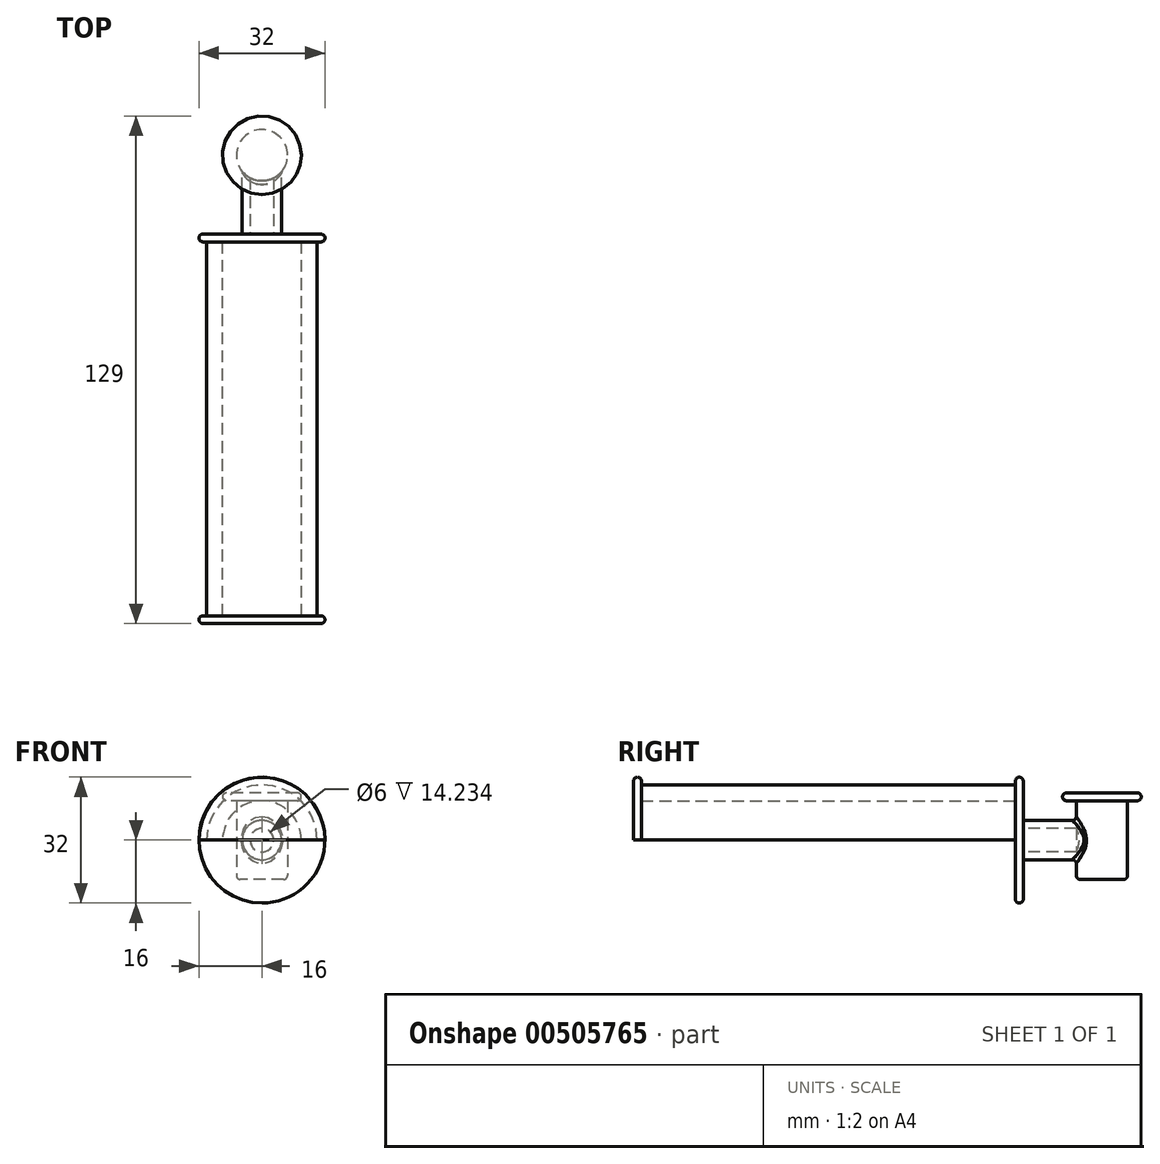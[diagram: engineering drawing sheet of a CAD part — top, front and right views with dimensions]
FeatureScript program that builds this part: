
annotation { "Feature Type Name" : "Feature", "Feature Type Description" : "" }
export const myFeature = defineFeature(function(context is Context, id is Id, definition is map)
    precondition{}
    {
        {
            var Q0;
            Q0=qCreatedBy(makeId("Top.planeOp"),FACE);
            var sketch = newSketch(context, id + "F0", { "sketchPlane" : qUnion([Q0])});
            skCircle(sketch, "E0", {"center": v(0, 0) * mm, "radius": 6.5 * mm});
            skSolve(sketch);
        }
        {
            var Q0;
            Q0 = qSketchRegion(id + "F0", true);
            extrude(context, id + "F1", {"entities" : qUnion([Q0]), "endBound" : BoundingType.SYMMETRIC, "depth" : 20 * mm});
        }
        {
            var Q0;
            Q0=makeQuery(id+"F1.opExtrude","CAP_FACE",FACE,{"disambiguationData":[OSD([sQuery(id+"F0.wireOp",EDGE,"E0")])],"isStart":false});
            var sketch = newSketch(context, id + "F2", { "sketchPlane" : qUnion([Q0])});
            skCircle(sketch, "E1", {"center": v(0, 0) * mm, "radius": 10 * mm});
            skSolve(sketch);
        }
        {
            var Q0;
            Q0 = qSketchRegion(id + "F2", true);
            extrude(context, id + "F3", {"entities" : qUnion([Q0]), "operationType" : NewBodyOperationType.ADD, "depth" : 2 * mm});
        }
        {
            var Q0;
            Q0=makeQuery(id+"F1.opExtrude","CAP_FACE",FACE,{"disambiguationData":[OSD([sQuery(id+"F0.wireOp",EDGE,"E0")])],"isStart":true});
            var sketch = newSketch(context, id + "F4", { "sketchPlane" : qUnion([Q0])});
            skCircle(sketch, "E2", {"center": v(0, 0) * mm, "radius": 10 * mm});
            skSolve(sketch);
        }
        {
            var Q0;
            Q0=qCreatedBy(makeId("Front.planeOp"),FACE);
            var sketch = newSketch(context, id + "F5", { "sketchPlane" : qUnion([Q0])});
            skCircle(sketch, "E3", {"center": v(0, 0) * mm, "radius": 5 * mm});
            skSolve(sketch);
        }
        {
            var Q0;
            Q0 = qSketchRegion(id + "F5", true);
            extrude(context, id + "F6", {"entities" : qUnion([Q0]), "operationType" : NewBodyOperationType.ADD, "depth" : 20 * mm});
        }
        {
            var Q0;
            Q0=makeQuery(id+"F6.opExtrude","CAP_FACE",FACE,{"disambiguationData":[OSD([sQuery(id+"F5.wireOp",EDGE,"E3")])],"isStart":false});
            var sketch = newSketch(context, id + "F7", { "sketchPlane" : qUnion([Q0])});
            skCircle(sketch, "E4", {"center": v(0, 0) * mm, "radius": 3 * mm});
            skSolve(sketch);
        }
        {
            var Q0;
            Q0 = qSketchRegion(id + "F7", true);
            var Q1;
            Q1=makeQuery(id+"F1.opExtrude","SWEPT_FACE",FACE,{"disambiguationData":[OSD([sQuery(id+"F0.wireOp",EDGE,"E0")])]});
            extrude(context, id + "F8", {"entities" : qUnion([Q0]), "operationType" : NewBodyOperationType.REMOVE, "endBound" : BoundingType.UP_TO_SURFACE, "oppositeDirection" : true, "endBoundEntityFace" : qUnion([Q1]), "depth" : 25 * mm});
        }
        {
            var Q0;
            Q0=makeQuery(id+"F6.opExtrude","CAP_FACE",FACE,{"disambiguationData":[OSD([sQuery(id+"F5.wireOp",EDGE,"E3")])],"isStart":false});
            var sketch = newSketch(context, id + "F9", { "sketchPlane" : qUnion([Q0])});
            skCircle(sketch, "E5", {"center": v(0, 0) * mm, "radius": 16 * mm});
            skSolve(sketch);
        }
        {
            var Q0;
            Q0 = qSketchRegion(id + "F9", true);
            extrude(context, id + "F10", {"entities" : qUnion([Q0]), "operationType" : NewBodyOperationType.ADD, "depth" : 2 * mm});
        }
        {
            var Q0;
            Q0=makeQuery(id+"F10.opExtrude","CAP_FACE",FACE,{"disambiguationData":[OSD([sQuery(id+"F9.wireOp",EDGE,"E5")])],"isStart":false});
            var sketch = newSketch(context, id + "F11", { "sketchPlane" : qUnion([Q0])});
            skArc(sketch, "E6", {"start": v(14, 0) * mm, "mid": v(0, 14) * mm, "end": v(-14, 0) * mm});
            skLineSegment(sketch, "E7", {"start": v(-10, 0) * mm, "end": v(-14, 0) * mm});
            skLineSegment(sketch, "E8", {"start": v(10, 0) * mm, "end": v(14, 0) * mm});
            skArc(sketch, "E9.0", {"start": v(10, 0) * mm, "mid": v(0, 10) * mm, "end": v(-10, 0) * mm});
            skSolve(sketch);
        }
        {
            var Q0;
            Q0 = qSketchRegion(id + "F11", true);
            extrude(context, id + "F12", {"entities" : qUnion([Q0]), "operationType" : NewBodyOperationType.ADD, "depth" : 95 * mm});
        }
        {
            var Q0;
            Q0=makeQuery(id+"F12.opExtrude","CAP_FACE",FACE,{"disambiguationData":[OSD([sQuery(id+"F11.wireOp",EDGE,"E6"),sQuery(id+"F11.wireOp",EDGE,"E7"),sQuery(id+"F11.wireOp",EDGE,"E8"),sQuery(id+"F11.wireOp",EDGE,"E9.0")])],"isStart":false});
            var sketch = newSketch(context, id + "F13", { "sketchPlane" : qUnion([Q0])});
            skArc(sketch, "E10", {"start": v(16, 0) * mm, "mid": v(0, 16) * mm, "end": v(-16, 0) * mm});
            skLineSegment(sketch, "E11", {"start": v(0, 0) * mm, "end": v(16, 0) * mm});
            skLineSegment(sketch, "E12", {"start": v(0, 0) * mm, "end": v(-16, 0) * mm});
            skSolve(sketch);
        }
        {
            var Q0;
            Q0 = qSketchRegion(id + "F13", true);
            extrude(context, id + "F14", {"entities" : qUnion([Q0]), "operationType" : NewBodyOperationType.ADD, "depth" : 2 * mm});
        }
        {
            var Q0;
            Q0=makeQuery(id+"F1.opExtrude","CAP_EDGE",EDGE,{"disambiguationData":[OSD([sQuery(id+"F0.wireOp",EDGE,"E0")])],"isStart":false});
            var Q1;
            Q1=makeQuery(id+"F1.opExtrude","CAP_EDGE",EDGE,{"disambiguationData":[OSD([sQuery(id+"F0.wireOp",EDGE,"E0")])],"isStart":true});
            var Q2;
            Q2=makeQuery(id+"F3.opExtrude","CAP_EDGE",EDGE,{"disambiguationData":[OSD([sQuery(id+"F2.wireOp",EDGE,"E1")])],"isStart":false});
            var Q3;
            Q3=makeQuery(id+"F3.opExtrude","CAP_EDGE",EDGE,{"disambiguationData":[OSD([sQuery(id+"F2.wireOp",EDGE,"E1")])],"isStart":true});
            var Q4;
            Q4=makeQuery(id+"F7Hb1qnxx9VSfp0_1.opExtrude","CAP_EDGE",EDGE,{"disambiguationData":[OSD([sQuery(id+"F4.wireOp",EDGE,"E2")])],"isStart":true});
            var Q5;
            Q5=makeQuery(id+"F7Hb1qnxx9VSfp0_1.opExtrude","CAP_EDGE",EDGE,{"disambiguationData":[OSD([sQuery(id+"F4.wireOp",EDGE,"E2")])],"isStart":false});
            var Q6;
            Q6=makeQuery(id+"F10.opExtrude","CAP_EDGE",EDGE,{"disambiguationData":[OSD([sQuery(id+"F9.wireOp",EDGE,"E5")])],"isStart":true});
            var Q7;
            Q7=makeQuery(id+"F10.opExtrude","CAP_EDGE",EDGE,{"disambiguationData":[OSD([sQuery(id+"F9.wireOp",EDGE,"E5")])],"isStart":false});
            var Q8;
            Q8=makeQuery(id+"F6.opExtrude","CAP_EDGE",EDGE,{"disambiguationData":[OSD([sQuery(id+"F5.wireOp",EDGE,"E3")])],"isStart":false});
            var Q9;
            Q9=makeQuery(id+"F6.boolean.opBoolean","INTERSECT",EDGE,{"disambiguationData":[OD(1.0)],"derivedFrom":[makeQuery(id+"F1.opExtrude","SWEPT_FACE",FACE,{"disambiguationData":[OSD([sQuery(id+"F0.wireOp",EDGE,"E0")])]}),makeQuery(id+"F6.opExtrude","SWEPT_FACE",FACE,{"disambiguationData":[OSD([sQuery(id+"F5.wireOp",EDGE,"E3")])]})]});
            var Q10;
            Q10=makeQuery(id+"F6.boolean.opBoolean","INTERSECT",EDGE,{"disambiguationData":[OD(0.0)],"derivedFrom":[makeQuery(id+"F1.opExtrude","SWEPT_FACE",FACE,{"disambiguationData":[OSD([sQuery(id+"F0.wireOp",EDGE,"E0")])]}),makeQuery(id+"F6.opExtrude","SWEPT_FACE",FACE,{"disambiguationData":[OSD([sQuery(id+"F5.wireOp",EDGE,"E3")])]})]});
            var Q11;
            Q11=makeQuery(id+"F14.opExtrude","CAP_EDGE",EDGE,{"disambiguationData":[OSD([sQuery(id+"F13.wireOp",EDGE,"E10")])],"isStart":false});
            var Q12;
            Q12=makeQuery(id+"F14.opExtrude","CAP_EDGE",EDGE,{"disambiguationData":[OSD([sQuery(id+"F13.wireOp",EDGE,"E10")])],"isStart":true});
            var Q13;
            Q13=makeQuery(id+"F12.opExtrude","CAP_EDGE",EDGE,{"disambiguationData":[OSD([sQuery(id+"F11.wireOp",EDGE,"E6")])],"isStart":false});
            var Q14;
            Q14=makeQuery(id+"F12.opExtrude","CAP_EDGE",EDGE,{"disambiguationData":[OSD([sQuery(id+"F11.wireOp",EDGE,"E6")])],"isStart":true});
            fillet(context, id + "F15", {"entities" : qUnion([Q0, Q1, Q2, Q3, Q4, Q5, Q6, Q7, Q8, Q9, Q10, Q11, Q12, Q13, Q14]), "radius" : 1 * mm, "tangentPropagation" : true, "allowEdgeOverflow" : false});
        }
    });
